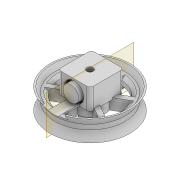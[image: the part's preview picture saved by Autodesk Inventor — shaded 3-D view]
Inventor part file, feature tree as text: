
AUTODESK INVENTOR PART (.ipt)
format: ipt  version: 2022 (Build 260153000, 153)  size: 478,720 bytes
history: native  units: mm
features: extrude x14, sketch x13, projected_geometry x11, chamfer x5, thicken_offset x2, plane x1, fillet x1
ambient origin geometry x8: Origin, YZ Plane, XZ Plane, XY Plane, X Axis, Y Axis, Z Axis, Center Point
bodies: Solid1 (feature_tree)
feature tree (47):
  extrude  "Extrusion1"  Depth=12.2mm
  extrude  "Extrusion2"  Depth=1.0mm
  extrude  "Extrusion3"  Depth=2.0mm TaperAngle=0.0deg
  plane  "Work Plane1"
  extrude  "Extrusion12"  Depth=10.0mm
  fillet  "Fillet5"  Radius=10.0mm
  extrude  "Extrusion14"  Depth=2.0mm
  extrude  "Extrusion15"  Depth=5.0mm TaperAngle=0.0deg
  extrude  "Extrusion16"  Depth=4.1mm
  extrude  "Extrusion17"  Depth=9.0mm
  sketch  "Sketch19"  dims[d79=3.0mm d80=2.0mm]
  extrude  "Extrusion18"  Depth=2.0mm
  extrude  "Extrusion19"  Depth=2.0mm
  thicken_offset  "Thicken1"
  extrude  "Extrusion20"  Depth=3.0mm TaperAngle=0.0deg
  extrude  "Extrusion21"  Depth=1.0mm
  chamfer  "Chamfer1"  Distance=2.0mm
  chamfer  "Chamfer2"  Distance=3.0mm
  chamfer  "Chamfer3"  Distance=2.0mm
  chamfer  "Chamfer4"  Distance=3.0mm
  sketch  "Sketch22"  dims[d86=4.1mm d87=2.0mm d88=3.0mm d89=2.0mm d90=3.0mm d91=2.4mm d92=0.0mm d94=17.0mm d95=2.0mm d96=0.0mm d97=1.5mm d98=2.0mm d99=0.0mm d100=100.0mm d101=0.0mm d102=12.0mm d103=12.0mm d104=3.0mm d105=3.0mm d106=0.0mm d107=3.0mm d108=8.0mm d109=8.0mm d110=3.0mm d111=0.0mm d112=3.0mm d113=5.0mm d114=45.0deg d115=3.0mm d116=5.0mm d117=45.0deg d118=2.0mm d119=3.0mm d120=45.0deg d121=2.0mm d122=3.0mm d123=45.0deg d124=37.0mm d125=19.0mm d126=1.5mm d127=1.5mm d128=30.0mm d130=360.0deg d132=6.0mm d133=0.0mm d134=8.0mm d135=0.0mm d136=2.0mm d137=2.0mm d138=45.0deg d139=2.0mm d140=2.0mm]
  extrude  "Extrusion22"  Depth=2.4mm TaperAngle=0.0deg
  extrude  "Extrusion23"  Depth=17.0mm
  chamfer  "Chamfer5"  Distance=2.0mm
  thicken_offset  "Thicken2"
  sketch  "Sketch1"  dims[d0=9.8mm d1=12.2mm]
  sketch  "Sketch2"  dims[d3=4.0mm d4=1.0mm]
  projected_geometry  "Projected Loop1"
  sketch  "Sketch3"  dims[d5=18.0mm d6=0.0mm d7=2.0mm d8=0.0mm]
  projected_geometry  "Projected Loop2"
  sketch  "Sketch6"  dims[d9=3.0mm d10=0.0mm d49=4.1mm d50=10.0mm]
  projected_geometry  "Projected Loop3"
  projected_geometry  "Projected Loop4"
  sketch  "Sketch14"  dims[d63=100.0mm d64=0.0mm d65=2.0mm]
  sketch  "Sketch15"  dims[d69=7.0mm d71=5.0mm d72=0.0mm]
  projected_geometry  "Projected Loop10"
  projected_geometry  "Projected Loop11"
  sketch  "Sketch16"  dims[d73=16.0mm d74=4.1mm]
  projected_geometry  "Projected Loop12"
  sketch  "Sketch17"  dims[d75=1.4mm d76=9.0mm]
  sketch  "Sketch18"  dims[d77=1.0mm d78=2.0mm]
  projected_geometry  "Projected Loop13"
  projected_geometry  "Projected Loop14"
  projected_geometry  "Projected Loop15"
  sketch  "Sketch20"  dims[d81=4.0mm d82=3.0mm d83=0.0mm]
  sketch  "Sketch21"  dims[d84=1.4mm d85=1.0mm]
  projected_geometry  "Projected Loop16"
